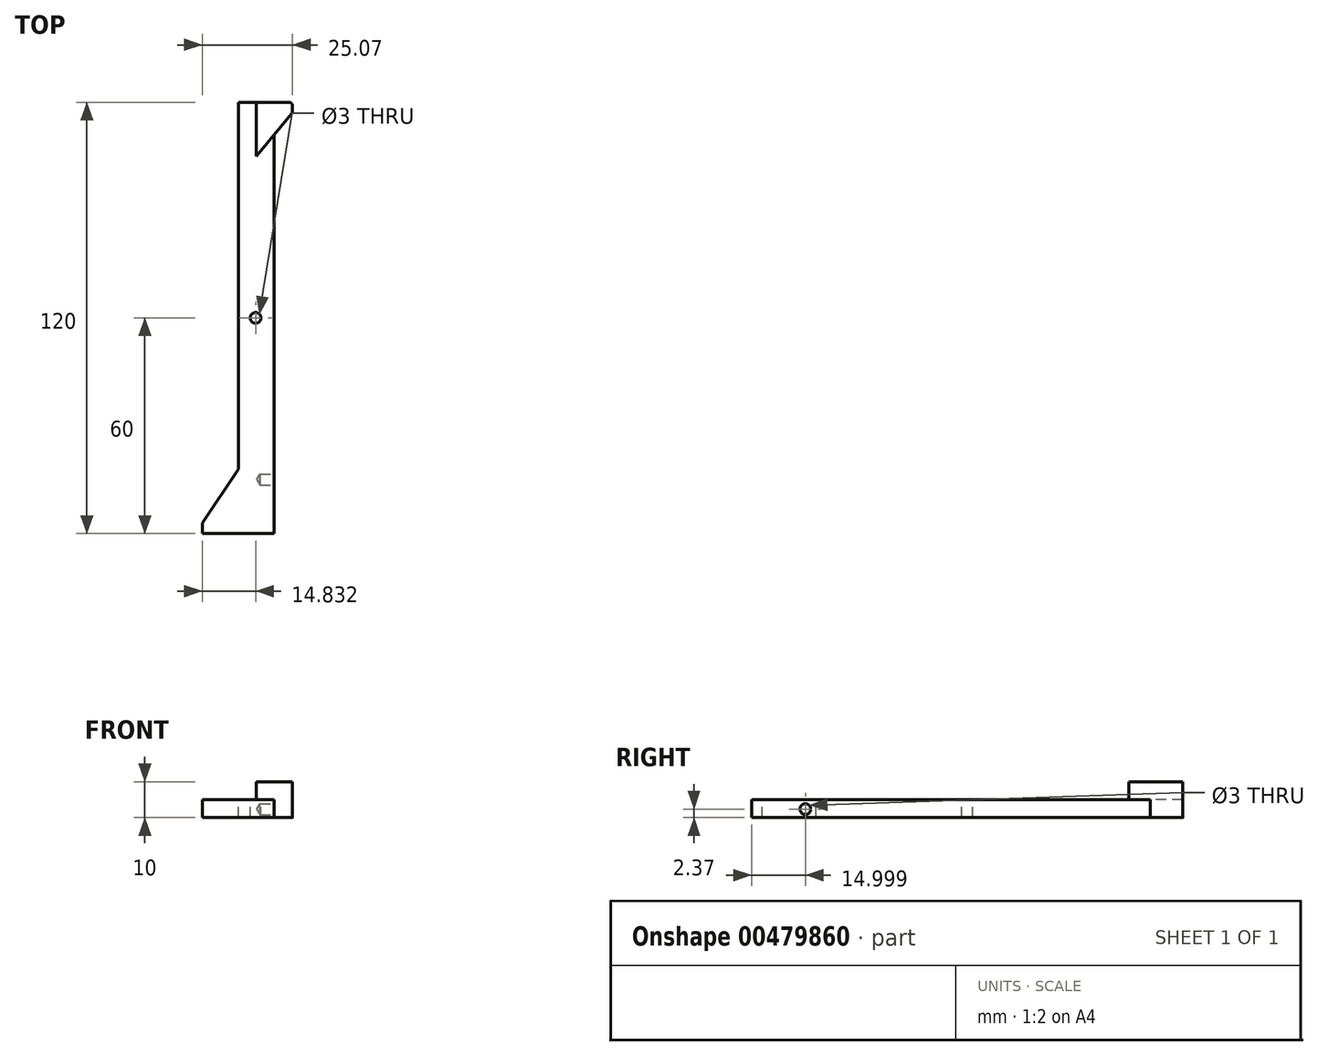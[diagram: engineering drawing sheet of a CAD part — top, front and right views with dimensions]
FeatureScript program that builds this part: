
annotation { "Feature Type Name" : "Feature", "Feature Type Description" : "" }
export const myFeature = defineFeature(function(context is Context, id is Id, definition is map)
    precondition{}
    {
        {
            var Q0;
            Q0=qCreatedBy(makeId("Right.planeOp"),FACE);
            var sketch = newSketch(context, id + "F0", { "sketchPlane" : qUnion([Q0])});
            skLineSegment(sketch, "E0.bottom", {"start": v(0, 5.07) * mm, "end": v(60, 5.07) * mm});
            skLineSegment(sketch, "E0.top", {"start": v(0, 15.07) * mm, "end": v(60, 15.07) * mm});
            skLineSegment(sketch, "E0.left", {"start": v(0, 5.07) * mm, "end": v(0, 15.07) * mm});
            skLineSegment(sketch, "E0.right", {"start": v(60, 5.07) * mm, "end": v(60, 15.07) * mm});
            skSolve(sketch);
        }
        {
            var Q0;
            Q0=makeQuery(id+"F0.imprint","IMPRINT",FACE,{"disambiguationData":[TD([[makeQuery(id+"F0.imprint","IMPRINT",EDGE,{"derivedFrom":sQuery(id+"F0.wireOp",EDGE,"E0.bottom")}),1.0]])]});
            extrude(context, id + "F1", {"entities" : qUnion([Q0]), "oppositeDirection" : true, "depth" : 5 * mm});
        }
        {
            var Q0;
            Q0=makeQuery(id+"F1.opExtrude","SWEPT_BODY",BODY,{"disambiguationData":[OSD([sQuery(id+"F0.wireOp",EDGE,"E0.bottom"),sQuery(id+"F0.wireOp",EDGE,"E0.top"),sQuery(id+"F0.wireOp",EDGE,"E0.left"),sQuery(id+"F0.wireOp",EDGE,"E0.right")])]});
            var Q1;
            Q1=qCreatedBy(makeId("Front.planeOp"),FACE);
            mirror(context, id + "F2", {"operationType" : NewBodyOperationType.ADD, "entities" : qUnion([Q0]), "mirrorPlane" : qUnion([Q1])});
        }
        {
            var Q0;
            Q0=qCreatedBy(makeId("Right.planeOp"),FACE);
            var sketch = newSketch(context, id + "F3", { "sketchPlane" : qUnion([Q0])});
            skLineSegment(sketch, "E1", {"start": v(-60, 15.07) * mm, "end": v(-60, 25.07) * mm});
            skLineSegment(sketch, "E2", {"start": v(-60, 25.07) * mm, "end": v(-57, 25.07) * mm});
            skLineSegment(sketch, "E3", {"start": v(-57, 25.07) * mm, "end": v(-42, 15.07) * mm});
            skLineSegment(sketch, "E4", {"start": v(-60, 15.07) * mm, "end": v(-42, 15.07) * mm});
            skSolve(sketch);
        }
        {
            var Q0;
            Q0=makeQuery(id+"F3.imprint","IMPRINT",FACE,{"disambiguationData":[TD([[makeQuery(id+"F3.imprint","IMPRINT",EDGE,{"derivedFrom":sQuery(id+"F3.wireOp",EDGE,"E1")}),-1.0]])]});
            extrude(context, id + "F4", {"entities" : qUnion([Q0]), "operationType" : NewBodyOperationType.ADD, "oppositeDirection" : true, "depth" : 5 * mm});
        }
        {
            var Q0;
            {var subQ0=makeQuery(id+"F1.opExtrude","CAP_FACE",FACE,{"disambiguationData":[OSD([sQuery(id+"F0.wireOp",EDGE,"E0.bottom"),sQuery(id+"F0.wireOp",EDGE,"E0.top"),sQuery(id+"F0.wireOp",EDGE,"E0.left"),sQuery(id+"F0.wireOp",EDGE,"E0.right")])],"isStart":true});Q0=makeQuery(id+"F4.boolean.opBoolean","MERGE",FACE,{"derivedFrom":[makeQuery(id+"F2.boolean.opBoolean","MERGE",FACE,{"derivedFrom":[subQ0,makeQuery(id+"F2.opPattern","COPY",FACE,{"derivedFrom":subQ0,"instanceName":"1"})]}),makeQuery(id+"F4.opExtrude","CAP_FACE",FACE,{"disambiguationData":[OSD([sQuery(id+"F3.wireOp",EDGE,"E1"),sQuery(id+"F3.wireOp",EDGE,"E2"),sQuery(id+"F3.wireOp",EDGE,"E3"),sQuery(id+"F3.wireOp",EDGE,"E4")])],"isStart":true})]});}
            var sketch = newSketch(context, id + "F5", { "sketchPlane" : qUnion([Q0])});
            skLineSegment(sketch, "E5", {"start": v(60, 0) * mm, "end": v(57, 0) * mm});
            skLineSegment(sketch, "E6.0", {"start": v(45, 10.07) * mm, "end": v(60, 10.07) * mm});
            skLineSegment(sketch, "E7", {"start": v(45, 10.07) * mm, "end": v(57, 0) * mm});
            skLineSegment(sketch, "E8", {"start": v(60, 10.07) * mm, "end": v(60, 0) * mm});
            skSolve(sketch);
        }
        {
            var Q0;
            Q0 = qSketchRegion(id + "F5", true);
            extrude(context, id + "F6", {"entities" : qUnion([Q0]), "depth" : 5 * mm});
        }
        {
            var Q0;
            Q0 = qSketchRegion(id + "F5", true);
            extrude(context, id + "F7", {"entities" : qUnion([Q0]), "oppositeDirection" : true, "depth" : 5 * mm});
        }
        {
            var Q0;
            {var subQ0=makeQuery(id+"F1.opExtrude","CAP_FACE",FACE,{"disambiguationData":[OSD([sQuery(id+"F0.wireOp",EDGE,"E0.bottom"),sQuery(id+"F0.wireOp",EDGE,"E0.top"),sQuery(id+"F0.wireOp",EDGE,"E0.left"),sQuery(id+"F0.wireOp",EDGE,"E0.right")])],"isStart":true});Q0=makeQuery(id+"F4.boolean.opBoolean","MERGE",FACE,{"derivedFrom":[makeQuery(id+"F2.boolean.opBoolean","MERGE",FACE,{"derivedFrom":[subQ0,makeQuery(id+"F2.opPattern","COPY",FACE,{"derivedFrom":subQ0,"instanceName":"1"})]}),makeQuery(id+"F4.opExtrude","CAP_FACE",FACE,{"disambiguationData":[OSD([sQuery(id+"F3.wireOp",EDGE,"E1"),sQuery(id+"F3.wireOp",EDGE,"E2"),sQuery(id+"F3.wireOp",EDGE,"E3"),sQuery(id+"F3.wireOp",EDGE,"E4")])],"isStart":true})]});}
            var sketch = newSketch(context, id + "F8", { "sketchPlane" : qUnion([Q0])});
            skCircle(sketch, "E9", {"center": v(0, 10.24) * mm, "radius": 1.5 * mm});
            skSolve(sketch);
        }
        {
            var Q0;
            Q0=sQuery(id+"F8.wireOp",VERTEX,"E9.center");
            var Q1;
            Q1=makeQuery(id+"F1.opExtrude","SWEPT_BODY",BODY,{"disambiguationData":[OSD([sQuery(id+"F0.wireOp",EDGE,"E0.bottom"),sQuery(id+"F0.wireOp",EDGE,"E0.top"),sQuery(id+"F0.wireOp",EDGE,"E0.left"),sQuery(id+"F0.wireOp",EDGE,"E0.right")])]});
            hole(context, id + "F9", {"style" : HoleStyle.SIMPLE, "endStyle" : HoleEndStyle.THROUGH, "holeDiameter" : 3 * mm, "isTappedThrough" : true, "tappedDepth" : 12 * mm, "tapClearance" : 3, "locations" : qUnion([Q0]), "scope" : qUnion([Q1])});
        }
        {
            var Q0;
            Q0=makeQuery(id+"F1.opExtrude","SWEPT_BODY",BODY,{"disambiguationData":[OSD([sQuery(id+"F0.wireOp",EDGE,"E0.bottom"),sQuery(id+"F0.wireOp",EDGE,"E0.top"),sQuery(id+"F0.wireOp",EDGE,"E0.left"),sQuery(id+"F0.wireOp",EDGE,"E0.right")])]});
            var Q1;
            Q1=makeQuery(id+"F6.opExtrude","SWEPT_BODY",BODY,{"disambiguationData":[OSD([sQuery(id+"F5.wireOp",EDGE,"UhboBd4w-R35A-0HcM-enAD-9fFz2IIVh9G9"),sQuery(id+"F5.wireOp",EDGE,"rB1Wc7Tp-oyV5-S23L-3Mj0-CaNdZQgc7ClD"),sQuery(id+"F5.wireOp",EDGE,"E5"),sQuery(id+"F5.wireOp",EDGE,"DJYZvtT0-Kbwy-thwd-GrK7-TRFbQ7qUNFli")])]});
            var Q2;
            Q2=makeQuery(id+"F7.opExtrude","SWEPT_BODY",BODY,{"disambiguationData":[OSD([sQuery(id+"F5.wireOp",EDGE,"UhboBd4w-R35A-0HcM-enAD-9fFz2IIVh9G9"),sQuery(id+"F5.wireOp",EDGE,"rB1Wc7Tp-oyV5-S23L-3Mj0-CaNdZQgc7ClD"),sQuery(id+"F5.wireOp",EDGE,"E5"),sQuery(id+"F5.wireOp",EDGE,"DJYZvtT0-Kbwy-thwd-GrK7-TRFbQ7qUNFli")])]});
            booleanBodies(context, id + "F10", {"operationType" : BooleanOperationType.UNION, "tools" : qUnion([Q0, Q1, Q2])});
        }
        {
            var Q0;
            {var subQ0=sQuery(id+"F5.wireOp",EDGE,"E7");var subQ1=sQuery(id+"F5.wireOp",EDGE,"E5");Q0=makeQuery(id+"F10.opBoolean","MERGE",EDGE,{"derivedFrom":[makeQuery(id+"F6.opExtrude","SWEPT_EDGE",EDGE,{"disambiguationData":[OSD([subQ1,subQ0])]}),makeQuery(id+"F7.opExtrude","SWEPT_EDGE",EDGE,{"disambiguationData":[OSD([subQ1,subQ0])]})]});}
            var Q1;
            {var subQ0=sQuery(id+"F5.wireOp",EDGE,"E8");var subQ1=sQuery(id+"F5.wireOp",EDGE,"E5");Q1=makeQuery(id+"F10.opBoolean","MERGE",EDGE,{"derivedFrom":[makeQuery(id+"F6.opExtrude","SWEPT_EDGE",EDGE,{"disambiguationData":[OSD([subQ1,subQ0])]}),makeQuery(id+"F7.opExtrude","SWEPT_EDGE",EDGE,{"disambiguationData":[OSD([subQ1,subQ0])]})]});}
            fillet(context, id + "F11", {"entities" : qUnion([Q0, Q1]), "radius" : 1 * mm, "tangentPropagation" : true, "allowEdgeOverflow" : false});
        }
        {
            var Q0;
            {var subQ0=makeQuery(id+"F1.opExtrude","SWEPT_FACE",FACE,{"disambiguationData":[OSD([sQuery(id+"F0.wireOp",EDGE,"E0.bottom")])]});Q0=makeQuery(id+"F2.boolean.opBoolean","MERGE",FACE,{"derivedFrom":[subQ0,makeQuery(id+"F2.opPattern","COPY",FACE,{"derivedFrom":subQ0,"instanceName":"1"})]});}
            var sketch = newSketch(context, id + "F12", { "sketchPlane" : qUnion([Q0])});
            skCircle(sketch, "E10", {"center": v(-2.63, 45) * mm, "radius": 1.5 * mm});
            skSolve(sketch);
        }
        {
            var Q0;
            Q0=sQuery(id+"F12.wireOp",VERTEX,"E10.center");
            var Q1;
            Q1=makeQuery(id+"F1.opExtrude","SWEPT_BODY",BODY,{"disambiguationData":[OSD([sQuery(id+"F0.wireOp",EDGE,"E0.bottom"),sQuery(id+"F0.wireOp",EDGE,"E0.top"),sQuery(id+"F0.wireOp",EDGE,"E0.left"),sQuery(id+"F0.wireOp",EDGE,"E0.right")])]});
            hole(context, id + "F13", {"style" : HoleStyle.SIMPLE, "endStyle" : HoleEndStyle.BLIND, "holeDiameter" : 3 * mm, "holeDepth" : 4 * mm, "isTappedThrough" : true, "tappedDepth" : 12 * mm, "tapClearance" : 3, "locations" : qUnion([Q0]), "scope" : qUnion([Q1])});
        }
        {
            var Q0;
            Q0=makeQuery(id+"F1.opExtrude","SWEPT_BODY",BODY,{"disambiguationData":[OSD([sQuery(id+"F0.wireOp",EDGE,"E0.bottom"),sQuery(id+"F0.wireOp",EDGE,"E0.top"),sQuery(id+"F0.wireOp",EDGE,"E0.left"),sQuery(id+"F0.wireOp",EDGE,"E0.right")])]});
            var Q1;
            {var subQ0=makeQuery(id+"F1.opExtrude","CAP_EDGE",EDGE,{"disambiguationData":[OSD([sQuery(id+"F0.wireOp",EDGE,"E0.top")])],"isStart":true});Q1=makeQuery(id+"F2.boolean.opBoolean","MERGE",EDGE,{"derivedFrom":[subQ0,makeQuery(id+"F2.opPattern","COPY",EDGE,{"derivedFrom":subQ0,"instanceName":"1"})]});}
            transform(context, id + "F14", {"entities" : qUnion([Q0]), "transformType" : TransformType.ROTATION, "transformAxis" : qUnion([Q1]), "angle" : 90 * degree, "oppositeDirection" : true, "makeCopy" : false});
        }
    });
